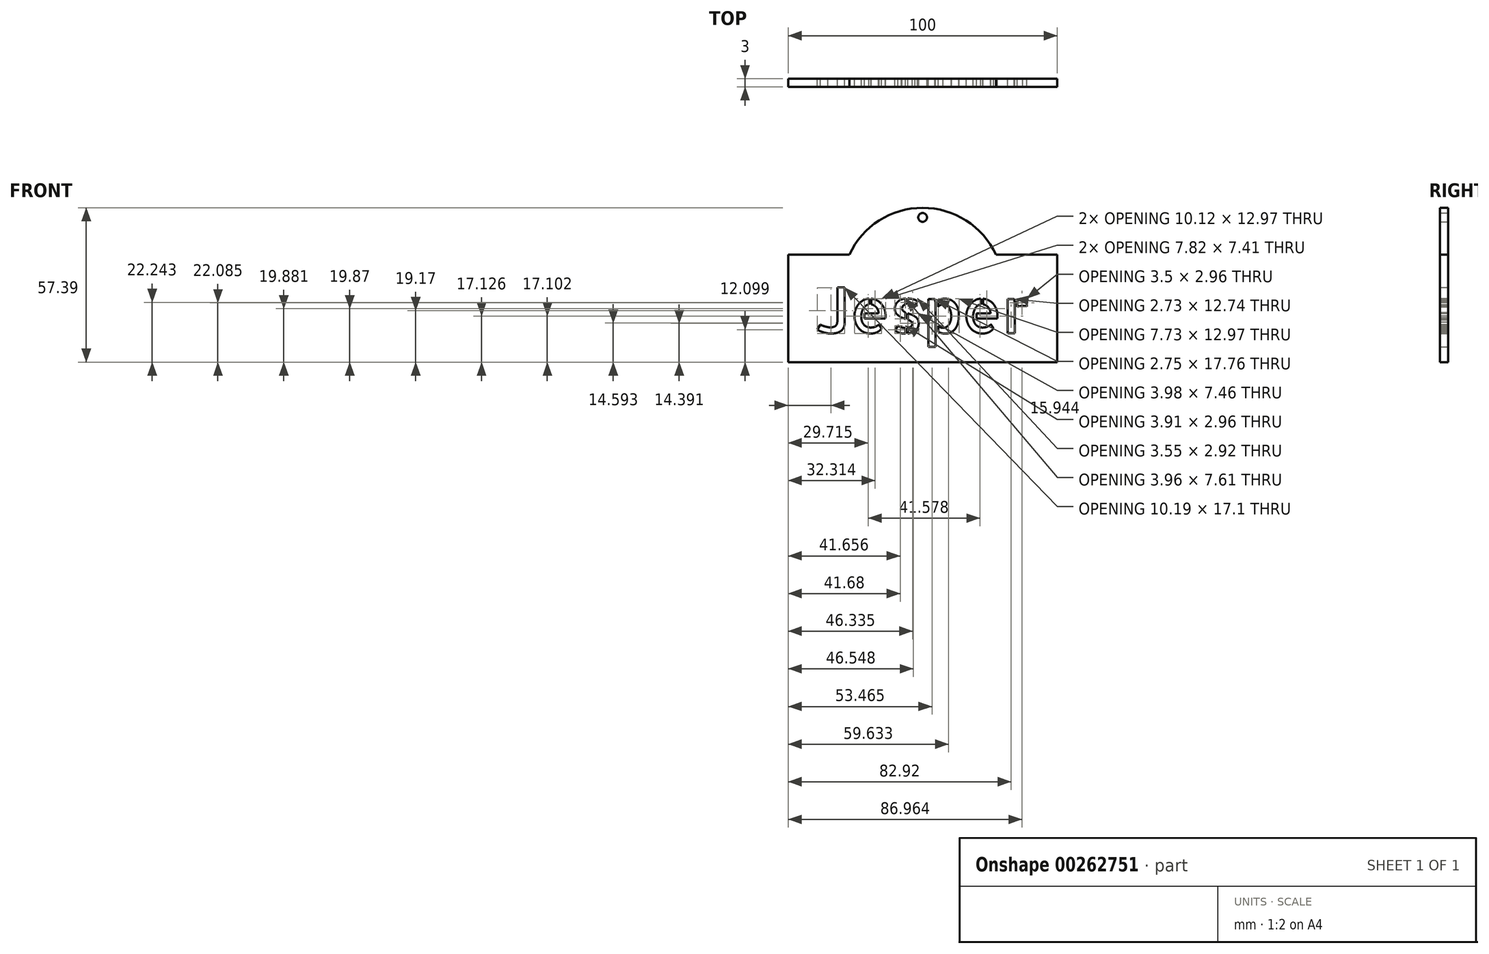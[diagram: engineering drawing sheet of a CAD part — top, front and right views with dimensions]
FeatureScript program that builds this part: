
annotation { "Feature Type Name" : "Feature", "Feature Type Description" : "" }
export const myFeature = defineFeature(function(context is Context, id is Id, definition is map)
    precondition{}
    {
        {
            var Q0;
            Q0=qCreatedBy(makeId("Front.planeOp"),FACE);
            var sketch = newSketch(context, id + "F0", { "sketchPlane" : qUnion([Q0])});
            skLineSegment(sketch, "E0.bottom", {"start": v(-54.73, 42.93) * mm, "end": v(45.27, 42.93) * mm});
            skLineSegment(sketch, "E0.top", {"start": v(-54.73, 2.95) * mm, "end": v(45.27, 2.95) * mm});
            skLineSegment(sketch, "E0.left", {"start": v(-54.73, 42.93) * mm, "end": v(-54.73, 2.95) * mm});
            skLineSegment(sketch, "E0.right", {"start": v(45.27, 42.93) * mm, "end": v(45.27, 2.95) * mm});
            skArc(sketch, "E1", {"start": v(22.5, 42.93) * mm, "mid": v(-4.73, 60.34) * mm, "end": v(-31.96, 42.93) * mm});
            skPoint(sketch, "E2", {"position": v(-4.73, 60.34) * mm});
            skPoint(sketch, "E3", {"position": v(-4.73, 42.93) * mm});
            skCircle(sketch, "E4", {"center": v(-4.73, 56.78) * mm, "radius": 1.63 * mm});
            skText(sketch, "E5", { "text": "Jesper", "fontName": "AllertaStencil-Regular.ttf"});
            const initialGuessF0  = {"E5": [-0.04447, 0.01368, 1, 0, 0.01666]};
            skSetInitialGuess(sketch, initialGuessF0);
            skSolve(sketch);
        }
        {
            var Q0;
            {var subQ0=sQuery(id+"F0.wireOp",EDGE,"E1");Q0=makeQuery(id+"F0.imprint","IMPRINT",FACE,{"disambiguationData":[TD([[makeQuery(id+"F0.imprint","IMPRINT",EDGE,{"derivedFrom":subQ0}),1.0]])]});}
            var Q1;
            Q1=makeQuery(id+"F0.imprint","IMPRINT",FACE,{"disambiguationData":[TD([[makeQuery(id+"F0.imprint","IMPRINT",EDGE,{"derivedFrom":sQuery(id+"F0.wireOp",EDGE,"E0.top")}),1.0]])]});
            extrude(context, id + "F1", {"entities" : qUnion([Q0, Q1]), "depth" : 3 * mm});
        }
    });
